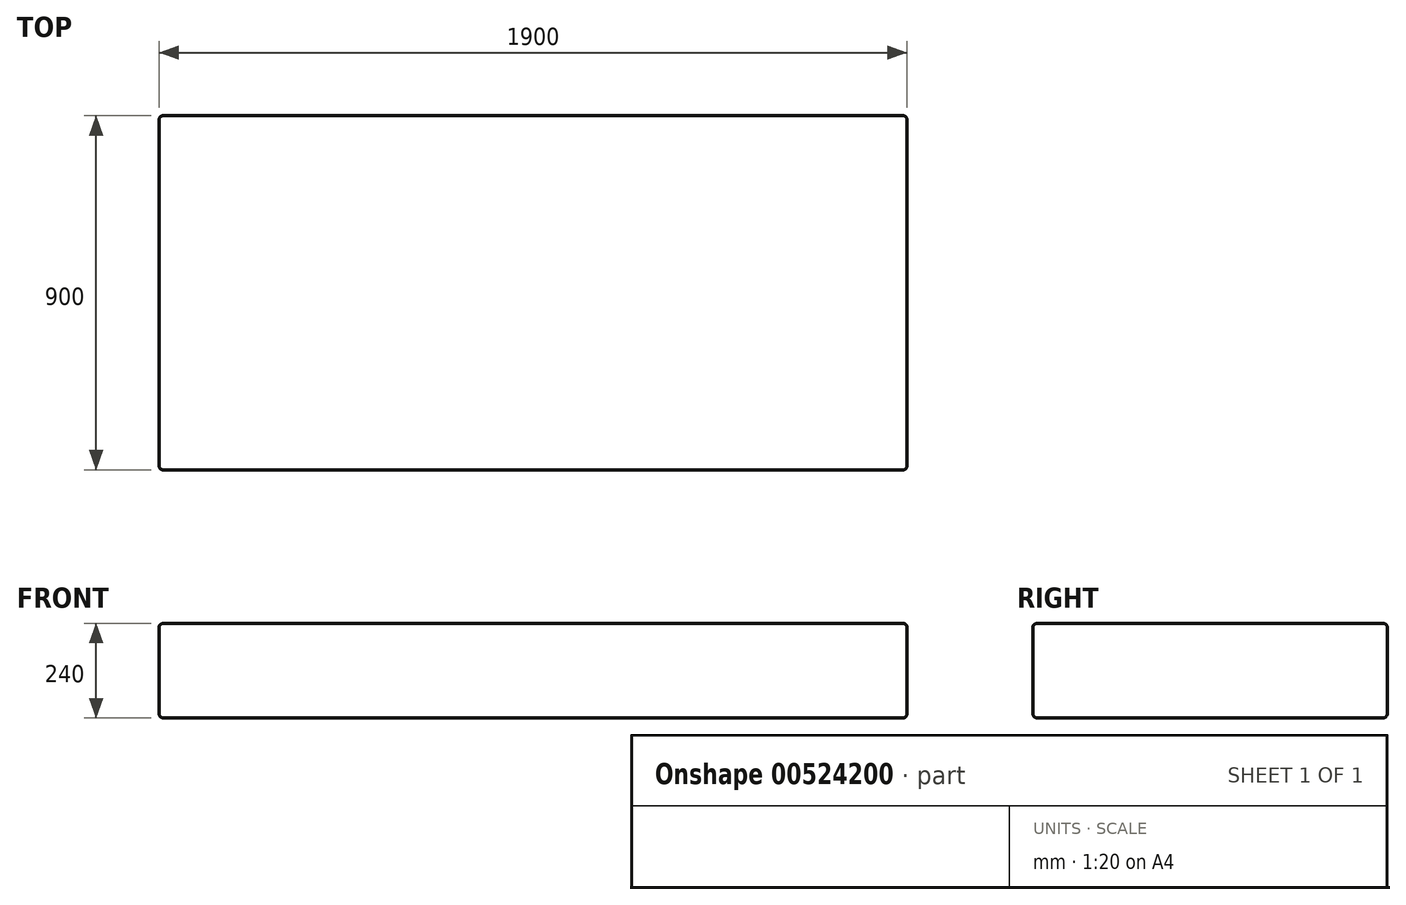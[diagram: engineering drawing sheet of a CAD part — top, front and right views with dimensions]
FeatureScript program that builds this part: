
annotation { "Feature Type Name" : "Feature", "Feature Type Description" : "" }
export const myFeature = defineFeature(function(context is Context, id is Id, definition is map)
    precondition{}
    {
        {
            var Q0;
            Q0=qCreatedBy(makeId("Top.planeOp"),FACE);
            var sketch = newSketch(context, id + "F0", { "sketchPlane" : qUnion([Q0])});
            skLineSegment(sketch, "E0.bottom", {"start": v(0, 0) * mm, "end": v(-1900, 0) * mm});
            skLineSegment(sketch, "E0.top", {"start": v(0, 900) * mm, "end": v(-1900, 900) * mm});
            skLineSegment(sketch, "E0.left", {"start": v(0, 0) * mm, "end": v(0, 900) * mm});
            skLineSegment(sketch, "E0.right", {"start": v(-1900, 0) * mm, "end": v(-1900, 900) * mm});
            skSolve(sketch);
        }
        {
            var Q0;
            Q0 = qSketchRegion(id + "F0", true);
            extrude(context, id + "F1", {"entities" : qUnion([Q0]), "depth" : 240 * mm, "offsetDistance" : 25 * mm});
        }
        {
            var Q0;
            Q0=makeQuery(id+"F1.opExtrude","SWEPT_EDGE",EDGE,{"disambiguationData":[OSD([sQuery(id+"F0.wireOp",EDGE,"E0.top"),sQuery(id+"F0.wireOp",EDGE,"E0.left")])]});
            var Q1;
            Q1=makeQuery(id+"F1.opExtrude","SWEPT_EDGE",EDGE,{"disambiguationData":[OSD([sQuery(id+"F0.wireOp",EDGE,"E0.top"),sQuery(id+"F0.wireOp",EDGE,"E0.right")])]});
            var Q2;
            Q2=makeQuery(id+"F1.opExtrude","SWEPT_EDGE",EDGE,{"disambiguationData":[OSD([sQuery(id+"F0.wireOp",EDGE,"E0.bottom"),sQuery(id+"F0.wireOp",EDGE,"E0.left")])]});
            var Q3;
            Q3=makeQuery(id+"F1.opExtrude","SWEPT_EDGE",EDGE,{"disambiguationData":[OSD([sQuery(id+"F0.wireOp",EDGE,"E0.bottom"),sQuery(id+"F0.wireOp",EDGE,"E0.right")])]});
            var Q4;
            Q4=makeQuery(id+"F1.opExtrude","CAP_EDGE",EDGE,{"disambiguationData":[OSD([sQuery(id+"F0.wireOp",EDGE,"E0.bottom")])],"isStart":true});
            var Q5;
            Q5=makeQuery(id+"F1.opExtrude","CAP_EDGE",EDGE,{"disambiguationData":[OSD([sQuery(id+"F0.wireOp",EDGE,"E0.left")])],"isStart":true});
            var Q6;
            Q6=makeQuery(id+"F1.opExtrude","CAP_EDGE",EDGE,{"disambiguationData":[OSD([sQuery(id+"F0.wireOp",EDGE,"E0.top")])],"isStart":true});
            var Q7;
            Q7=makeQuery(id+"F1.opExtrude","CAP_EDGE",EDGE,{"disambiguationData":[OSD([sQuery(id+"F0.wireOp",EDGE,"E0.right")])],"isStart":true});
            var Q8;
            Q8=makeQuery(id+"F1.opExtrude","CAP_EDGE",EDGE,{"disambiguationData":[OSD([sQuery(id+"F0.wireOp",EDGE,"E0.bottom")])],"isStart":false});
            var Q9;
            Q9=makeQuery(id+"F1.opExtrude","CAP_EDGE",EDGE,{"disambiguationData":[OSD([sQuery(id+"F0.wireOp",EDGE,"E0.left")])],"isStart":false});
            var Q10;
            Q10=makeQuery(id+"F1.opExtrude","CAP_EDGE",EDGE,{"disambiguationData":[OSD([sQuery(id+"F0.wireOp",EDGE,"E0.top")])],"isStart":false});
            var Q11;
            Q11=makeQuery(id+"F1.opExtrude","CAP_EDGE",EDGE,{"disambiguationData":[OSD([sQuery(id+"F0.wireOp",EDGE,"E0.right")])],"isStart":false});
            fillet(context, id + "F2", {"entities" : qUnion([Q0, Q1, Q2, Q3, Q4, Q5, Q6, Q7, Q8, Q9, Q10, Q11]), "radius" : 10 * mm, "tangentPropagation" : true, "allowEdgeOverflow" : false});
        }
    });
